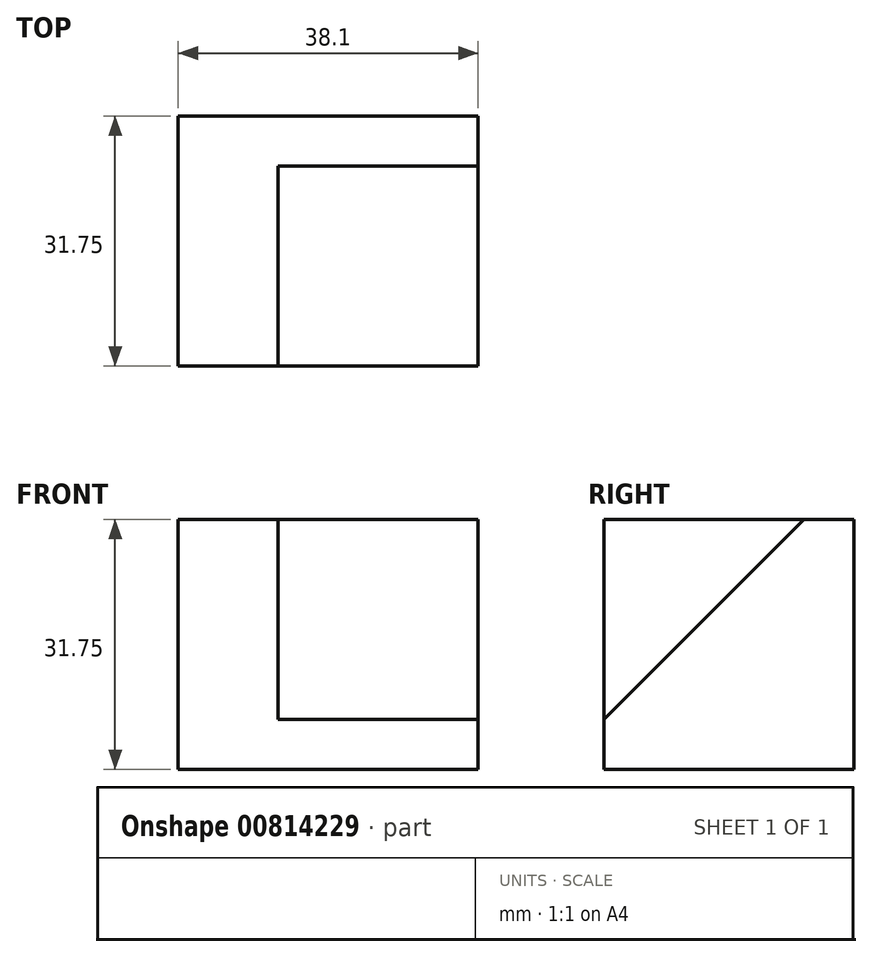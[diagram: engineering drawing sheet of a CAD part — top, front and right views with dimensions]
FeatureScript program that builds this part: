
annotation { "Feature Type Name" : "Feature", "Feature Type Description" : "" }
export const myFeature = defineFeature(function(context is Context, id is Id, definition is map)
    precondition{}
    {
        {
            var Q0;
            Q0=qCreatedBy(makeId("Top.planeOp"),FACE);
            var sketch = newSketch(context, id + "F0", { "sketchPlane" : qUnion([Q0])});
            skLineSegment(sketch, "E0", {"start": v(0, 0) * mm, "end": v(0, 31.75) * mm});
            skLineSegment(sketch, "E1", {"start": v(0, 0) * mm, "end": v(38.1, 0) * mm});
            skLineSegment(sketch, "E2", {"start": v(38.1, 0) * mm, "end": v(38.1, 31.75) * mm});
            skLineSegment(sketch, "E3", {"start": v(38.1, 31.75) * mm, "end": v(0, 31.75) * mm});
            skSolve(sketch);
        }
        {
            var Q0;
            Q0=makeQuery(id+"F0.imprint","IMPRINT",FACE,{"disambiguationData":[TD([[makeQuery(id+"F0.imprint","IMPRINT",EDGE,{"derivedFrom":sQuery(id+"F0.wireOp",EDGE,"E0")}),-1.0]])]});
            extrude(context, id + "F1", {"entities" : qUnion([Q0]), "depth" : 31.75 * mm, "offsetDistance" : 25.4 * mm});
        }
        {
            var Q0;
            Q0=makeQuery(id+"F1.opExtrude","SWEPT_FACE",FACE,{"disambiguationData":[OSD([sQuery(id+"F0.wireOp",EDGE,"E2")])]});
            var sketch = newSketch(context, id + "F2", { "sketchPlane" : qUnion([Q0])});
            skLineSegment(sketch, "E4", {"start": v(31.75, 31.75) * mm, "end": v(25.4, 31.75) * mm});
            skLineSegment(sketch, "E5", {"start": v(0, 0) * mm, "end": v(0, 6.35) * mm});
            skLineSegment(sketch, "E6", {"start": v(0, 6.35) * mm, "end": v(25.4, 31.75) * mm});
            skSolve(sketch);
        }
        {
            var Q0;
            {var subQ0=sQuery(id+"F2.wireOp",EDGE,"E6");Q0=makeQuery(id+"F2.imprint","IMPRINT",FACE,{"disambiguationData":[TD([[makeQuery(id+"F2.imprint","IMPRINT",EDGE,{"derivedFrom":subQ0}),1.0]])]});}
            extrude(context, id + "F3", {"entities" : qUnion([Q0]), "operationType" : NewBodyOperationType.REMOVE, "oppositeDirection" : true, "depth" : 25.4 * mm, "offsetDistance" : 25.4 * mm});
        }
    });
